# Revit family: QF_BOURGEAT_CARAVANE_Meubles_buffet_bain_marie_baie_libre_simple_accès
name_source: partatom
category: Equipement spécialisé
revit_build: Autodesk Revit 2015 (Build: 20140606_1530(x64)
units: mm (PartAtom-declared; Revit-internal decimal feet)

## types (3) — shared parameters
Fabricant = BOURGEAT
Fréquence = 50 Hz
Hauteur hors tout = 1385 mm  [stored 4.54396 ft]
Hauteur plan de travail = 839 mm  [stored 2.75262 ft]
Indice de protection = 33
Inox = Acier inoxydable, poli
Intensité nominale = 9 A
Phase = 2
Plastique noir = Plastique, noir
Profondeur hors tout = 840 mm  [stored 2.75591 ft]
Tension = 230 V
URL catalogue = http://www.bourgeat.fr
Vitro = Verre vitro

## per-type parameters (varying)
| type | 4GN | Bac4 | Charge max | Charge maximale | Longueur de la tablette | Longueur hors tout | Longueur pare-haleine | Mixte | Modèle | NonMixte | Poids net à vide | Poids à vide | Puissance électrique  | Spécification du Fabricant |
| Modèle simple accès 3 GN | Non | Non | 90.00 kg | 90 kg | 1055 mm | 1315 mm  [stored 4.3143 ft] | 1080 mm | Non | 857013 | Oui | 140.00 kg | 140 kg | 2100 W | Meuble buffet bain-marie -baie libre |
| Modèle simple accès 4 GN Mixte | Oui | Non | 100.00 kg | 100 kg | 1380 mm  [stored 4.52756 ft] | 1640 mm  [stored 5.38058 ft] | 1405 mm  [stored 4.60958 ft] | Oui | 857514 | Non | 200.00 kg | 200 kg | 2180 W | Meuble buffet bain marie + plaque chauffante -baie libre |
| Modéle simple accès 4GN | Oui | Oui | 120.00 kg | 120 kg | 1380 mm  [stored 4.52756 ft] | 1640 mm  [stored 5.38058 ft] | 1405 mm  [stored 4.60958 ft] | Non | 857014 | Oui | 160.00 kg | 160 kg | 2100 W | Meuble buffet bain marie -baie libre |

note: [stored X ft] marks values corroborated as IEEE doubles in the binary element streams (Revit-internal decimal feet)

## geometry (parser evidence)
native form markers: Blend x4
no freeform markers — native parametric forms only
